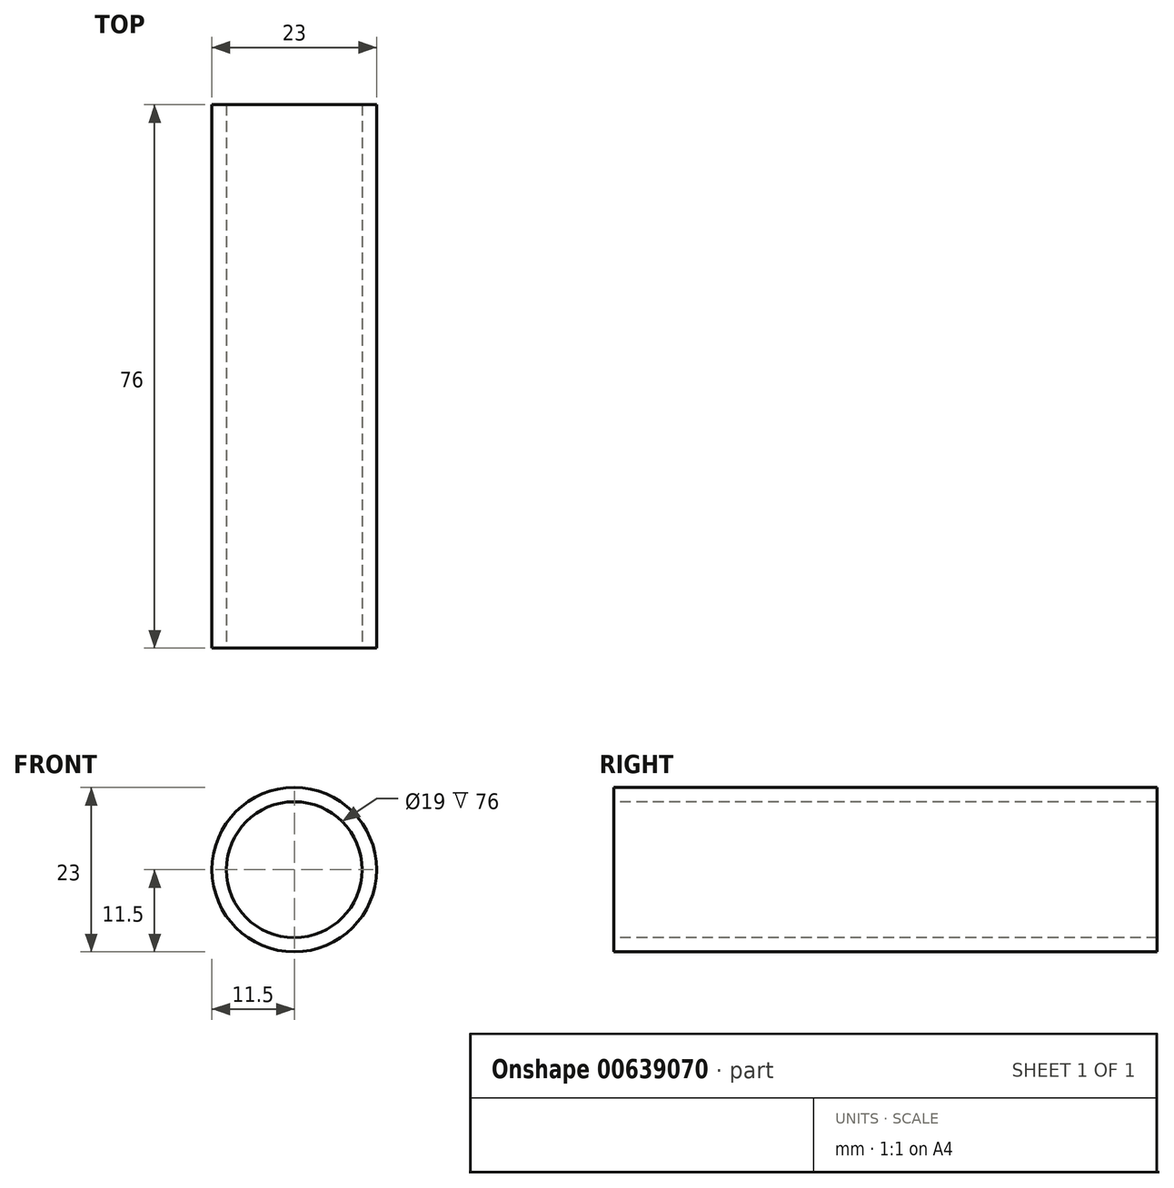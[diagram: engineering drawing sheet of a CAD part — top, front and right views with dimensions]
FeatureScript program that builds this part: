
annotation { "Feature Type Name" : "Feature", "Feature Type Description" : "" }
export const myFeature = defineFeature(function(context is Context, id is Id, definition is map)
    precondition{}
    {
        {
            var Q0;
            Q0=qCreatedBy(makeId("Right.planeOp"),FACE);
            var sketch = newSketch(context, id + "F0", { "sketchPlane" : qUnion([Q0])});
            skLineSegment(sketch, "E0.bottom", {"start": v(38, -9.5) * mm, "end": v(-38, -9.5) * mm});
            skLineSegment(sketch, "E0.top", {"start": v(38, -11.5) * mm, "end": v(-38, -11.5) * mm});
            skLineSegment(sketch, "E0.left", {"start": v(38, -9.5) * mm, "end": v(38, -11.5) * mm});
            skLineSegment(sketch, "E0.right", {"start": v(-38, -9.5) * mm, "end": v(-38, -11.5) * mm});
            skPoint(sketch, "E0.middle", {"position": v(0, -10.5) * mm});
            skLineSegment(sketch, "E1", {"start": v(-37.06, 0) * mm, "end": v(42.24, 0) * mm});
            skSolve(sketch);
        }
        {
            var Q0;
            Q0=makeQuery(id+"F0.imprint","IMPRINT",FACE,{"disambiguationData":[TD([[makeQuery(id+"F0.imprint","IMPRINT",EDGE,{"derivedFrom":sQuery(id+"F0.wireOp",EDGE,"E0.bottom")}),1.0]])]});
            var Q1;
            Q1=sQuery(id+"F0.wireOp",EDGE,"E1");
            revolve(context, id + "F1", {"entities" : qUnion([Q0]), "axis" : qUnion([Q1]), "revolveType" : RevolveType.FULL});
        }
    });
